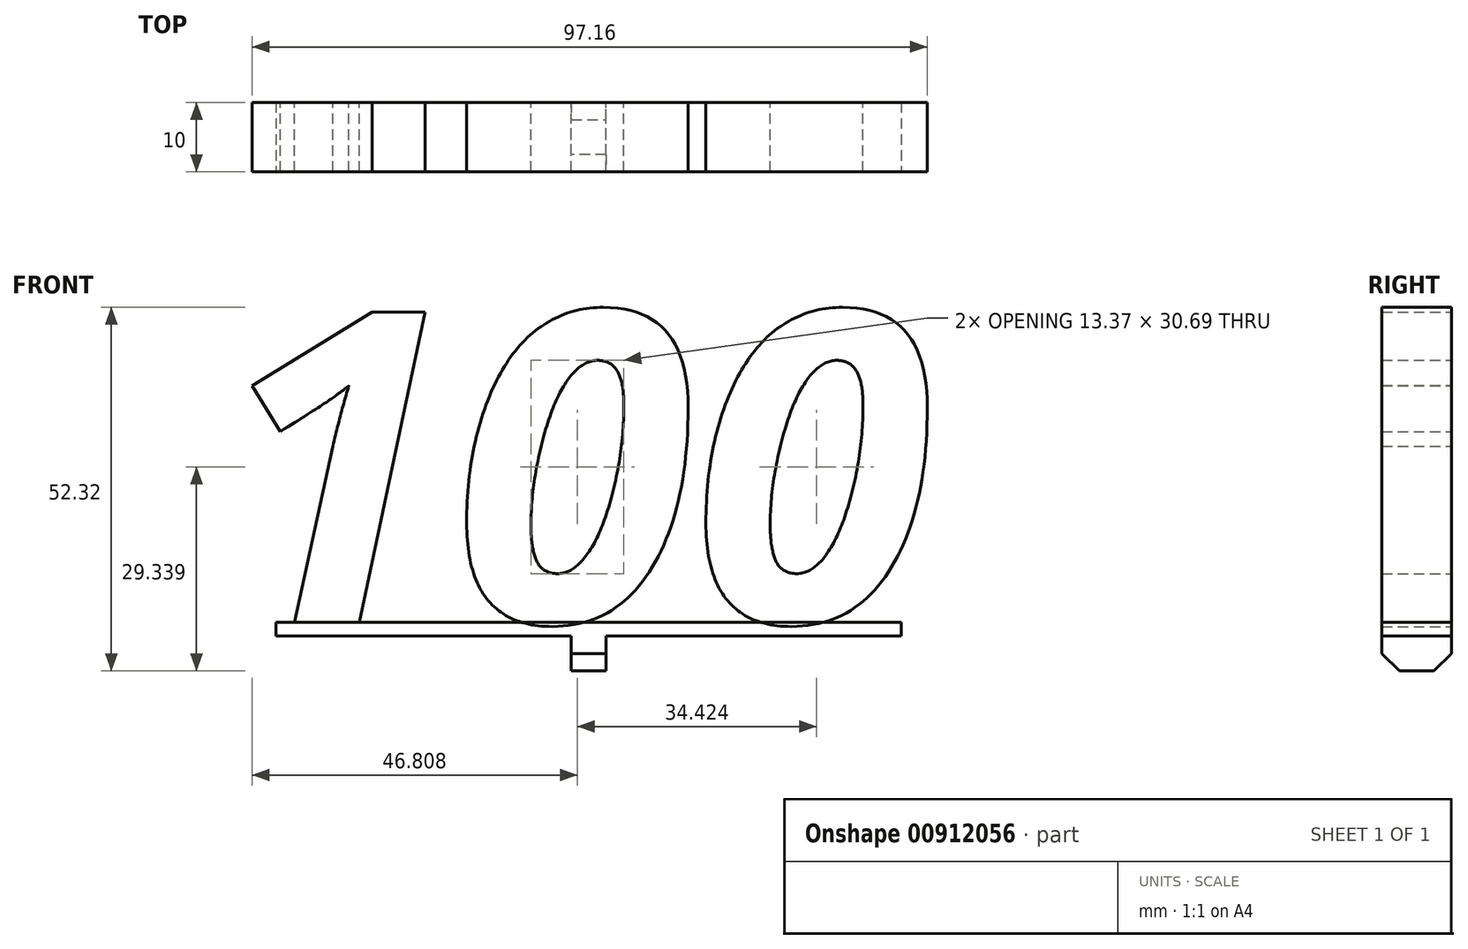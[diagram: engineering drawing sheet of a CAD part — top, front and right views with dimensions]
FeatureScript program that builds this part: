
annotation { "Feature Type Name" : "Feature", "Feature Type Description" : "" }
export const myFeature = defineFeature(function(context is Context, id is Id, definition is map)
    precondition{}
    {
        {
            var Q0;
            Q0=qCreatedBy(makeId("Front.planeOp"),FACE);
            var sketch = newSketch(context, id + "F0", { "sketchPlane" : qUnion([Q0])});
            skText(sketch, "E0", { "text": "100", "fontName": "OpenSans-BoldItalic.ttf"});
            const initialGuessF0  = {"E0": [-0.054, 0, 1, 0, 0.045]};
            skSetInitialGuess(sketch, initialGuessF0);
            skSolve(sketch);
        }
        {
            var Q0;
            Q0 = qSketchRegion(id + "F0", true);
            extrude(context, id + "F1", {"entities" : qUnion([Q0]), "endBound" : BoundingType.SYMMETRIC, "depth" : 10 * mm, "offsetDistance" : 25 * mm});
        }
        {
            var Q0;
            Q0=qCreatedBy(makeId("Top.planeOp"),FACE);
            var sketch = newSketch(context, id + "F2", { "sketchPlane" : qUnion([Q0])});
            skLineSegment(sketch, "E1.bottom", {"start": v(-45, 5) * mm, "end": v(45, 5) * mm});
            skLineSegment(sketch, "E1.top", {"start": v(-45, -5) * mm, "end": v(45, -5) * mm});
            skLineSegment(sketch, "E1.left", {"start": v(-45, 5) * mm, "end": v(-45, -5) * mm});
            skLineSegment(sketch, "E1.right", {"start": v(45, 5) * mm, "end": v(45, -5) * mm});
            skSolve(sketch);
        }
        {
            var Q0;
            Q0 = qSketchRegion(id + "F2", true);
            extrude(context, id + "F3", {"entities" : qUnion([Q0]), "oppositeDirection" : true, "depth" : 2 * mm, "offsetDistance" : 25 * mm});
        }
        {
            var Q0;
            Q0=makeQuery(id+"F3.opExtrude","CAP_FACE",FACE,{"disambiguationData":[OSD([sQuery(id+"F2.wireOp",EDGE,"E1.bottom"),sQuery(id+"F2.wireOp",EDGE,"E1.top"),sQuery(id+"F2.wireOp",EDGE,"E1.left"),sQuery(id+"F2.wireOp",EDGE,"E1.right")])],"isStart":false});
            var sketch = newSketch(context, id + "F4", { "sketchPlane" : qUnion([Q0])});
            skLineSegment(sketch, "E2.bottom", {"start": v(2.5, 5) * mm, "end": v(-2.5, 5) * mm});
            skLineSegment(sketch, "E2.top", {"start": v(2.5, -5) * mm, "end": v(-2.5, -5) * mm});
            skLineSegment(sketch, "E2.left", {"start": v(2.5, 5) * mm, "end": v(2.5, -5) * mm});
            skLineSegment(sketch, "E2.right", {"start": v(-2.5, 5) * mm, "end": v(-2.5, -5) * mm});
            skLineSegment(sketch, "E3", {"start": v(0, 5) * mm, "end": v(0, -5) * mm, "construction": true});
            skSolve(sketch);
        }
        {
            var Q0;
            Q0 = qSketchRegion(id + "F4", true);
            extrude(context, id + "F5", {"entities" : qUnion([Q0]), "operationType" : NewBodyOperationType.ADD, "depth" : 5 * mm, "offsetDistance" : 25 * mm});
        }
        {
            var Q0;
            Q0=makeQuery(id+"F5.opExtrude","CAP_EDGE",EDGE,{"disambiguationData":[OSD([sQuery(id+"F4.wireOp",EDGE,"E2.bottom")])],"isStart":false});
            var Q1;
            Q1=makeQuery(id+"F5.opExtrude","CAP_EDGE",EDGE,{"disambiguationData":[OSD([sQuery(id+"F4.wireOp",EDGE,"E2.top")])],"isStart":false});
            chamfer(context, id + "F6", {"entities" : qUnion([Q0, Q1]), "width" : 2.5 * mm, "tangentPropagation" : true});
        }
    });
